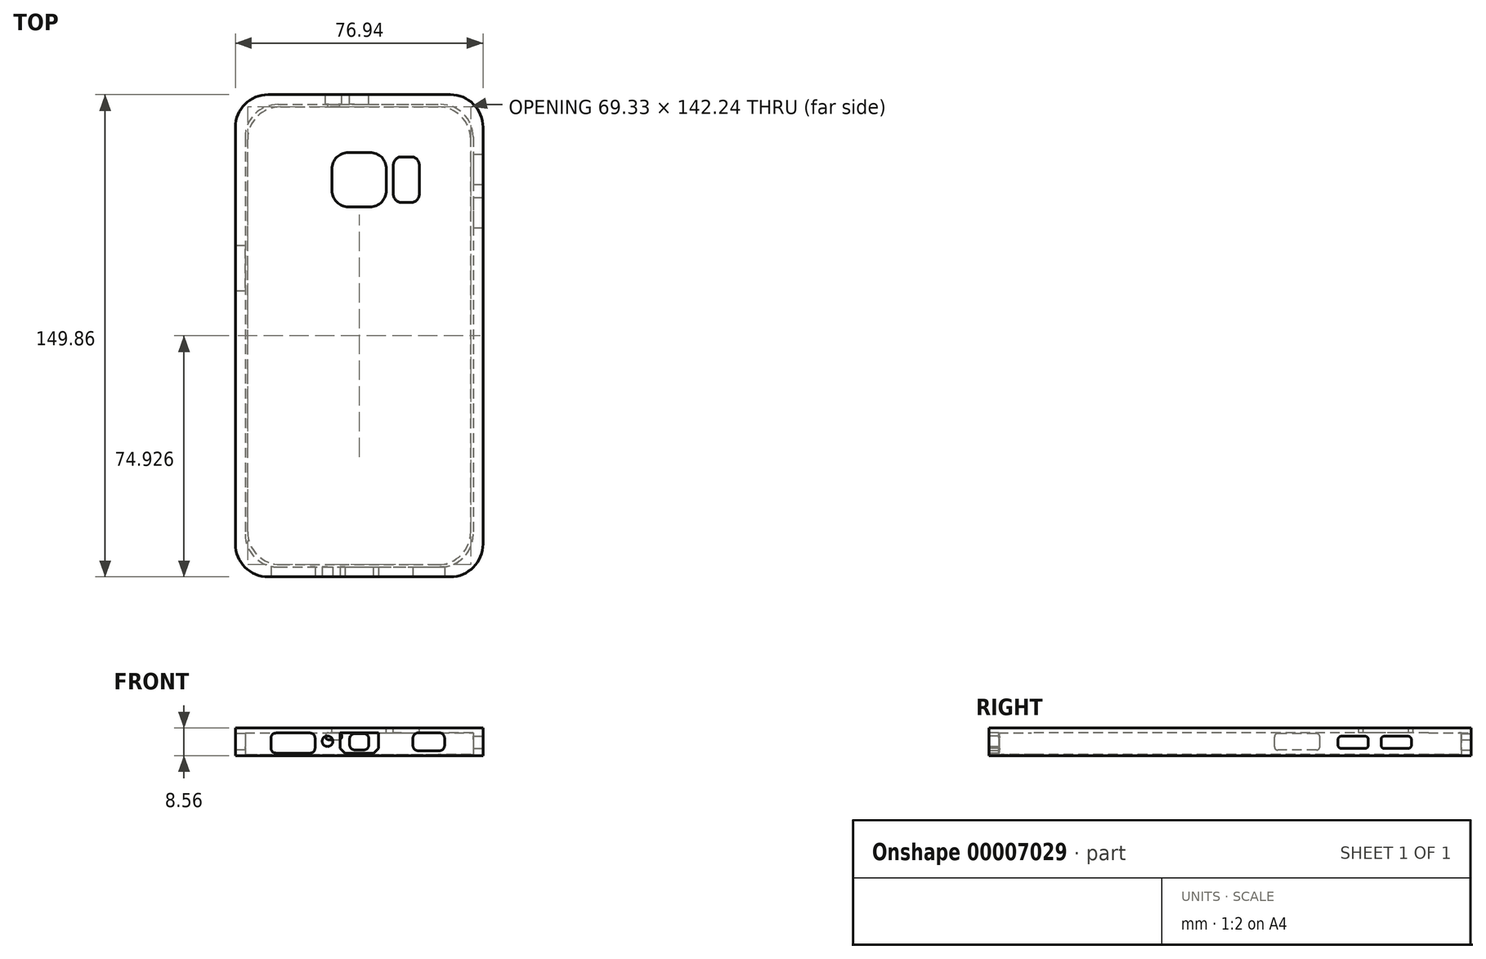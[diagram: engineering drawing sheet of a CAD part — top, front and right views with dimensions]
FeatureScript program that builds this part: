
annotation { "Feature Type Name" : "Feature", "Feature Type Description" : "" }
export const myFeature = defineFeature(function(context is Context, id is Id, definition is map)
    precondition{}
    {
        {
            var Q0;
            Q0=qCreatedBy(makeId("Top.planeOp"),FACE);
            var sketch = newSketch(context, id + "F0", { "sketchPlane" : qUnion([Q0])});
            skLineSegment(sketch, "E0.bottom", {"start": v(-42.48, 64.65) * mm, "end": v(28.37, 64.65) * mm});
            skLineSegment(sketch, "E0.top", {"start": v(-42.48, -79.12) * mm, "end": v(28.37, -79.12) * mm});
            skLineSegment(sketch, "E0.left", {"start": v(-42.48, 64.65) * mm, "end": v(-42.48, -79.12) * mm});
            skLineSegment(sketch, "E0.right", {"start": v(28.37, 64.65) * mm, "end": v(28.37, -79.12) * mm});
            skLineSegment(sketch, "E1.bottom", {"start": v(-45.53, 67.7) * mm, "end": v(31.41, 67.7) * mm});
            skLineSegment(sketch, "E1.top", {"start": v(-45.53, -82.16) * mm, "end": v(31.41, -82.16) * mm});
            skLineSegment(sketch, "E1.left", {"start": v(-45.53, 67.7) * mm, "end": v(-45.53, -82.16) * mm});
            skLineSegment(sketch, "E1.right", {"start": v(31.41, 67.7) * mm, "end": v(31.41, -82.16) * mm});
            skPoint(sketch, "E2", {"position": v(-7.06, 67.7) * mm});
            skPoint(sketch, "E3", {"position": v(-7.06, 64.65) * mm});
            skLineSegment(sketch, "E4", {"start": v(-7.06, 67.7) * mm, "end": v(-7.06, 64.65) * mm, "construction": true});
            skLineSegment(sketch, "E5", {"start": v(-7.06, -79.12) * mm, "end": v(-7.06, -82.16) * mm, "construction": true});
            skLineSegment(sketch, "E6", {"start": v(28.37, -7.23) * mm, "end": v(31.41, -7.23) * mm, "construction": true});
            skLineSegment(sketch, "E7", {"start": v(-42.48, -7.23) * mm, "end": v(-45.53, -7.23) * mm, "construction": true});
            skLineSegment(sketch, "E8.bottom", {"start": v(-31.56, -78.35) * mm, "end": v(17.44, -78.35) * mm});
            skLineSegment(sketch, "E8.top", {"start": v(-31.56, 63.89) * mm, "end": v(17.44, 63.89) * mm});
            skLineSegment(sketch, "E8.left", {"start": v(-41.72, -68.2) * mm, "end": v(-41.72, 53.73) * mm});
            skLineSegment(sketch, "E8.right", {"start": v(27.6, -68.2) * mm, "end": v(27.6, 53.73) * mm});
            skLineSegment(sketch, "E9", {"start": v(-7.06, -79.12) * mm, "end": v(-7.06, -78.35) * mm, "construction": true});
            skLineSegment(sketch, "E10", {"start": v(28.37, -7.23) * mm, "end": v(27.6, -7.23) * mm, "construction": true});
            skPoint(sketch, "E11.visualSharp", {"position": v(27.6, -78.35) * mm});
            skArc(sketch, "E11.filletArc", {"start": v(17.44, -78.35) * mm, "mid": v(24.63, -75.38) * mm, "end": v(27.6, -68.2) * mm});
            skPoint(sketch, "E12.visualSharp", {"position": v(-41.72, -78.35) * mm});
            skArc(sketch, "E12.filletArc", {"start": v(-41.72, -68.2) * mm, "mid": v(-38.75, -75.38) * mm, "end": v(-31.56, -78.35) * mm});
            skPoint(sketch, "E13.visualSharp", {"position": v(-41.72, 63.89) * mm});
            skArc(sketch, "E13.filletArc", {"start": v(-31.56, 63.89) * mm, "mid": v(-38.75, 60.91) * mm, "end": v(-41.72, 53.73) * mm});
            skPoint(sketch, "E14.visualSharp", {"position": v(27.6, 63.89) * mm});
            skArc(sketch, "E14.filletArc", {"start": v(27.6, 53.73) * mm, "mid": v(24.63, 60.91) * mm, "end": v(17.44, 63.89) * mm});
            skSolve(sketch);
        }
        {
            var Q0;
            Q0 = qSketchRegion(id + "F0", true);
            var Q1;
            Q1=makeQuery(id+"F0.imprint","IMPRINT",FACE,{"disambiguationData":[TD([[makeQuery(id+"F0.imprint","IMPRINT",EDGE,{"derivedFrom":sQuery(id+"F0.wireOp",EDGE,"E8.bottom")}),1.0]])]});
            var Q2;
            Q2=makeQuery(id+"F0.imprint","IMPRINT",FACE,{"disambiguationData":[TD([[makeQuery(id+"F0.imprint","IMPRINT",EDGE,{"derivedFrom":sQuery(id+"F0.wireOp",EDGE,"E0.bottom")}),-1.0]])]});
            extrude(context, id + "F1", {"entities" : qUnion([Q0, Q1, Q2]), "depth" : 8.56 * mm});
        }
        {
            var Q0;
            Q0=makeQuery(id+"F0.imprint","IMPRINT",FACE,{"disambiguationData":[TD([[makeQuery(id+"F0.imprint","IMPRINT",EDGE,{"derivedFrom":sQuery(id+"F0.wireOp",EDGE,"E8.bottom")}),1.0]])]});
            var Q1;
            Q1=makeQuery(id+"F0.imprint","IMPRINT",FACE,{"disambiguationData":[TD([[makeQuery(id+"F0.imprint","IMPRINT",EDGE,{"derivedFrom":sQuery(id+"F0.wireOp",EDGE,"E0.bottom")}),-1.0]])]});
            extrude(context, id + "F2", {"entities" : qUnion([Q0, Q1]), "operationType" : NewBodyOperationType.REMOVE, "depth" : 7.04 * mm});
        }
        {
            var Q0;
            Q0=makeQuery(id+"F2.boolean.opBoolean","COPY",EDGE,{"derivedFrom":makeQuery(id+"F2.opExtrude","SWEPT_EDGE",EDGE,{"disambiguationData":[OSD([sQuery(id+"F0.wireOp",EDGE,"E8.bottom"),sQuery(id+"F0.wireOp",EDGE,"E8.left")])]})});
            var Q1;
            Q1=makeQuery(id+"F2.boolean.opBoolean","COPY",EDGE,{"derivedFrom":makeQuery(id+"F2.opExtrude","SWEPT_EDGE",EDGE,{"disambiguationData":[OSD([sQuery(id+"F0.wireOp",EDGE,"E8.bottom"),sQuery(id+"F0.wireOp",EDGE,"E8.right")])]})});
            var Q2;
            Q2=makeQuery(id+"F2.boolean.opBoolean","COPY",EDGE,{"derivedFrom":makeQuery(id+"F2.opExtrude","SWEPT_EDGE",EDGE,{"disambiguationData":[OSD([sQuery(id+"F0.wireOp",EDGE,"E8.top"),sQuery(id+"F0.wireOp",EDGE,"E8.left")])]})});
            var Q3;
            Q3=makeQuery(id+"F2.boolean.opBoolean","COPY",EDGE,{"derivedFrom":makeQuery(id+"F2.opExtrude","SWEPT_EDGE",EDGE,{"disambiguationData":[OSD([sQuery(id+"F0.wireOp",EDGE,"E8.top"),sQuery(id+"F0.wireOp",EDGE,"E8.right")])]})});
            var Q4;
            Q4=makeQuery(id+"F1.opExtrude","SWEPT_EDGE",EDGE,{"disambiguationData":[OSD([sQuery(id+"F0.wireOp",EDGE,"E1.bottom"),sQuery(id+"F0.wireOp",EDGE,"E1.right")])]});
            var Q5;
            Q5=makeQuery(id+"F1.opExtrude","SWEPT_EDGE",EDGE,{"disambiguationData":[OSD([sQuery(id+"F0.wireOp",EDGE,"E1.top"),sQuery(id+"F0.wireOp",EDGE,"E1.right")])]});
            var Q6;
            Q6=makeQuery(id+"F1.opExtrude","SWEPT_EDGE",EDGE,{"disambiguationData":[OSD([sQuery(id+"F0.wireOp",EDGE,"E1.top"),sQuery(id+"F0.wireOp",EDGE,"E1.left")])]});
            var Q7;
            Q7=makeQuery(id+"F1.opExtrude","SWEPT_EDGE",EDGE,{"disambiguationData":[OSD([sQuery(id+"F0.wireOp",EDGE,"E1.bottom"),sQuery(id+"F0.wireOp",EDGE,"E1.left")])]});
            var Q8;
            Q8=makeQuery(id+"F2.boolean.opBoolean","COPY",EDGE,{"derivedFrom":makeQuery(id+"F2.opExtrude","SWEPT_EDGE",EDGE,{"disambiguationData":[OSD([sQuery(id+"F0.wireOp",EDGE,"E0.bottom"),sQuery(id+"F0.wireOp",EDGE,"E0.right")])]})});
            var Q9;
            Q9=makeQuery(id+"F2.boolean.opBoolean","COPY",EDGE,{"derivedFrom":makeQuery(id+"F2.opExtrude","SWEPT_EDGE",EDGE,{"disambiguationData":[OSD([sQuery(id+"F0.wireOp",EDGE,"E0.bottom"),sQuery(id+"F0.wireOp",EDGE,"E0.left")])]})});
            var Q10;
            Q10=makeQuery(id+"F2.boolean.opBoolean","COPY",EDGE,{"derivedFrom":makeQuery(id+"F2.opExtrude","SWEPT_EDGE",EDGE,{"disambiguationData":[OSD([sQuery(id+"F0.wireOp",EDGE,"E0.top"),sQuery(id+"F0.wireOp",EDGE,"E0.left")])]})});
            var Q11;
            Q11=makeQuery(id+"F2.boolean.opBoolean","COPY",EDGE,{"derivedFrom":makeQuery(id+"F2.opExtrude","SWEPT_EDGE",EDGE,{"disambiguationData":[OSD([sQuery(id+"F0.wireOp",EDGE,"E0.top"),sQuery(id+"F0.wireOp",EDGE,"E0.right")])]})});
            fillet(context, id + "F3", {"entities" : qUnion([Q0, Q1, Q2, Q3, Q4, Q5, Q6, Q7, Q8, Q9, Q10, Q11]), "radius" : 10.16 * mm, "tangentPropagation" : true, "allowEdgeOverflow" : false});
        }
        {
            var Q0;
            Q0=makeQuery(id+"F0.imprint","IMPRINT",FACE,{"disambiguationData":[TD([[makeQuery(id+"F0.imprint","IMPRINT",EDGE,{"derivedFrom":sQuery(id+"F0.wireOp",EDGE,"E0.bottom")}),-1.0]])]});
            extrude(context, id + "F4", {"entities" : qUnion([Q0]), "operationType" : NewBodyOperationType.ADD, "depth" : 0.38 * mm});
        }
        {
            var Q0;
            Q0=makeQuery(id+"F1.opExtrude","CAP_FACE",FACE,{"disambiguationData":[OSD([sQuery(id+"F0.wireOp",EDGE,"E1.bottom"),sQuery(id+"F0.wireOp",EDGE,"E1.top"),sQuery(id+"F0.wireOp",EDGE,"E1.left"),sQuery(id+"F0.wireOp",EDGE,"E1.right")])],"isStart":false});
            var sketch = newSketch(context, id + "F5", { "sketchPlane" : qUnion([Q0])});
            skLineSegment(sketch, "E15.bottom", {"start": v(-15.5, 49.71) * mm, "end": v(1.39, 49.71) * mm});
            skLineSegment(sketch, "E15.top", {"start": v(-15.5, 32.82) * mm, "end": v(1.39, 32.82) * mm});
            skLineSegment(sketch, "E15.left", {"start": v(-15.5, 49.71) * mm, "end": v(-15.5, 32.82) * mm});
            skLineSegment(sketch, "E15.right", {"start": v(1.39, 49.71) * mm, "end": v(1.39, 32.82) * mm});
            skLineSegment(sketch, "E16", {"start": v(-15.5, 41.27) * mm, "end": v(-45.53, 41.27) * mm, "construction": true});
            skLineSegment(sketch, "E17", {"start": v(1.39, 41.27) * mm, "end": v(31.41, 41.27) * mm, "construction": true});
            skLineSegment(sketch, "E18.bottom", {"start": v(3.55, 48.34) * mm, "end": v(11.62, 48.34) * mm});
            skLineSegment(sketch, "E18.top", {"start": v(3.55, 34.2) * mm, "end": v(11.62, 34.2) * mm});
            skLineSegment(sketch, "E18.left", {"start": v(3.55, 48.34) * mm, "end": v(3.55, 34.2) * mm});
            skLineSegment(sketch, "E18.right", {"start": v(11.62, 48.34) * mm, "end": v(11.62, 34.2) * mm});
            skLineSegment(sketch, "E19", {"start": v(8.73, 48.34) * mm, "end": v(8.73, 41.27) * mm, "construction": true});
            skLineSegment(sketch, "E20", {"start": v(4.69, 41.27) * mm, "end": v(4.69, 34.2) * mm, "construction": true});
            skSolve(sketch);
        }
        {
            var Q0;
            Q0 = qSketchRegion(id + "F5", true);
            extrude(context, id + "F6", {"entities" : qUnion([Q0]), "operationType" : NewBodyOperationType.REMOVE, "oppositeDirection" : true, "depth" : 25.4 * mm});
        }
        {
            var Q0;
            Q0=makeQuery(id+"F6.boolean.opBoolean","COPY",EDGE,{"derivedFrom":makeQuery(id+"F6.opExtrude","SWEPT_EDGE",EDGE,{"disambiguationData":[OSD([sQuery(id+"F5.wireOp",EDGE,"E15.bottom"),sQuery(id+"F5.wireOp",EDGE,"E15.left")])]})});
            var Q1;
            Q1=makeQuery(id+"F6.boolean.opBoolean","COPY",EDGE,{"derivedFrom":makeQuery(id+"F6.opExtrude","SWEPT_EDGE",EDGE,{"disambiguationData":[OSD([sQuery(id+"F5.wireOp",EDGE,"E15.bottom"),sQuery(id+"F5.wireOp",EDGE,"E15.right")])]})});
            var Q2;
            Q2=makeQuery(id+"F6.boolean.opBoolean","COPY",EDGE,{"derivedFrom":makeQuery(id+"F6.opExtrude","SWEPT_EDGE",EDGE,{"disambiguationData":[OSD([sQuery(id+"F5.wireOp",EDGE,"E15.top"),sQuery(id+"F5.wireOp",EDGE,"E15.right")])]})});
            var Q3;
            Q3=makeQuery(id+"F6.boolean.opBoolean","COPY",EDGE,{"derivedFrom":makeQuery(id+"F6.opExtrude","SWEPT_EDGE",EDGE,{"disambiguationData":[OSD([sQuery(id+"F5.wireOp",EDGE,"E15.top"),sQuery(id+"F5.wireOp",EDGE,"E15.left")])]})});
            fillet(context, id + "F7", {"entities" : qUnion([Q0, Q1, Q2, Q3]), "radius" : 5.08 * mm, "tangentPropagation" : true, "allowEdgeOverflow" : false});
        }
        {
            var Q0;
            Q0=makeQuery(id+"F6.boolean.opBoolean","COPY",EDGE,{"derivedFrom":makeQuery(id+"F6.opExtrude","SWEPT_EDGE",EDGE,{"disambiguationData":[OSD([sQuery(id+"F5.wireOp",EDGE,"E18.bottom"),sQuery(id+"F5.wireOp",EDGE,"E18.right")])]})});
            var Q1;
            Q1=makeQuery(id+"F6.boolean.opBoolean","COPY",EDGE,{"derivedFrom":makeQuery(id+"F6.opExtrude","SWEPT_EDGE",EDGE,{"disambiguationData":[OSD([sQuery(id+"F5.wireOp",EDGE,"E18.bottom"),sQuery(id+"F5.wireOp",EDGE,"E18.left")])]})});
            var Q2;
            Q2=makeQuery(id+"F6.boolean.opBoolean","COPY",EDGE,{"derivedFrom":makeQuery(id+"F6.opExtrude","SWEPT_EDGE",EDGE,{"disambiguationData":[OSD([sQuery(id+"F5.wireOp",EDGE,"E18.top"),sQuery(id+"F5.wireOp",EDGE,"E18.right")])]})});
            var Q3;
            Q3=makeQuery(id+"F6.boolean.opBoolean","COPY",EDGE,{"derivedFrom":makeQuery(id+"F6.opExtrude","SWEPT_EDGE",EDGE,{"disambiguationData":[OSD([sQuery(id+"F5.wireOp",EDGE,"E18.top"),sQuery(id+"F5.wireOp",EDGE,"E18.left")])]})});
            fillet(context, id + "F8", {"entities" : qUnion([Q0, Q1, Q2, Q3]), "radius" : 2.54 * mm, "tangentPropagation" : true, "allowEdgeOverflow" : false});
        }
        {
            var Q0;
            Q0=makeQuery(id+"F1.opExtrude","SWEPT_FACE",FACE,{"disambiguationData":[OSD([sQuery(id+"F0.wireOp",EDGE,"E1.left")])]});
            var sketch = newSketch(context, id + "F9", { "sketchPlane" : qUnion([Q0])});
            skLineSegment(sketch, "E21.bottom", {"start": v(-20.68, 1.74) * mm, "end": v(-6.58, 1.74) * mm});
            skLineSegment(sketch, "E21.top", {"start": v(-20.68, 6.82) * mm, "end": v(-6.58, 6.82) * mm});
            skLineSegment(sketch, "E21.left", {"start": v(-20.68, 1.74) * mm, "end": v(-20.68, 6.82) * mm});
            skLineSegment(sketch, "E21.right", {"start": v(-6.58, 1.74) * mm, "end": v(-6.58, 6.82) * mm});
            skLineSegment(sketch, "E22", {"start": v(-13.63, 6.82) * mm, "end": v(-13.63, 8.56) * mm, "construction": true});
            skLineSegment(sketch, "E23", {"start": v(-13.63, 1.74) * mm, "end": v(-13.63, 0) * mm, "construction": true});
            skSolve(sketch);
        }
        {
            var Q0;
            Q0 = qSketchRegion(id + "F9", true);
            extrude(context, id + "F10", {"entities" : qUnion([Q0]), "operationType" : NewBodyOperationType.REMOVE, "oppositeDirection" : true, "depth" : 25.4 * mm});
        }
        {
            var Q0;
            Q0=makeQuery(id+"F10.boolean.opBoolean","COPY",EDGE,{"derivedFrom":makeQuery(id+"F10.opExtrude","SWEPT_EDGE",EDGE,{"disambiguationData":[OSD([sQuery(id+"F9.wireOp",EDGE,"E21.bottom"),sQuery(id+"F9.wireOp",EDGE,"E21.left")])]})});
            var Q1;
            Q1=makeQuery(id+"F10.boolean.opBoolean","COPY",EDGE,{"derivedFrom":makeQuery(id+"F10.opExtrude","SWEPT_EDGE",EDGE,{"disambiguationData":[OSD([sQuery(id+"F9.wireOp",EDGE,"E21.top"),sQuery(id+"F9.wireOp",EDGE,"E21.left")])]})});
            var Q2;
            Q2=makeQuery(id+"F10.boolean.opBoolean","COPY",EDGE,{"derivedFrom":makeQuery(id+"F10.opExtrude","SWEPT_EDGE",EDGE,{"disambiguationData":[OSD([sQuery(id+"F9.wireOp",EDGE,"E21.bottom"),sQuery(id+"F9.wireOp",EDGE,"E21.right")])]})});
            var Q3;
            Q3=makeQuery(id+"F10.boolean.opBoolean","COPY",EDGE,{"derivedFrom":makeQuery(id+"F10.opExtrude","SWEPT_EDGE",EDGE,{"disambiguationData":[OSD([sQuery(id+"F9.wireOp",EDGE,"E21.top"),sQuery(id+"F9.wireOp",EDGE,"E21.right")])]})});
            fillet(context, id + "F11", {"entities" : qUnion([Q0, Q1, Q2, Q3]), "radius" : 1.02 * mm, "tangentPropagation" : true, "allowEdgeOverflow" : false});
        }
        {
            var Q0;
            Q0=makeQuery(id+"F1.opExtrude","SWEPT_FACE",FACE,{"disambiguationData":[OSD([sQuery(id+"F0.wireOp",EDGE,"E1.top")])]});
            var sketch = newSketch(context, id + "F12", { "sketchPlane" : qUnion([Q0])});
            skLineSegment(sketch, "E24.bottom", {"start": v(-1.09, 0.76) * mm, "end": v(-13.03, 0.76) * mm});
            skLineSegment(sketch, "E24.top", {"start": v(-1.09, 7.04) * mm, "end": v(-13.03, 7.04) * mm});
            skLineSegment(sketch, "E24.left", {"start": v(-1.09, 0.76) * mm, "end": v(-1.09, 7.04) * mm});
            skLineSegment(sketch, "E24.right", {"start": v(-13.03, 0.76) * mm, "end": v(-13.03, 7.04) * mm});
            skLineSegment(sketch, "E25", {"start": v(-45.53, 0) * mm, "end": v(-45.53, 7.04) * mm, "construction": true});
            skLineSegment(sketch, "E26", {"start": v(31.41, 7.04) * mm, "end": v(31.41, 0) * mm, "construction": true});
            skLineSegment(sketch, "E27", {"start": v(-45.53, 7.04) * mm, "end": v(31.41, 7.04) * mm, "construction": true});
            skPoint(sketch, "E28", {"position": v(-7.06, 7.04) * mm});
            skCircle(sketch, "E29", {"center": v(-16.9, 4.46) * mm, "radius": 1.65 * mm});
            skLineSegment(sketch, "E30", {"start": v(-45.53, 3.52) * mm, "end": v(31.41, 3.52) * mm, "construction": true});
            skLineSegment(sketch, "E31.bottom", {"start": v(-20.8, 0.77) * mm, "end": v(-34.48, 0.77) * mm});
            skLineSegment(sketch, "E31.top", {"start": v(-20.8, 7) * mm, "end": v(-34.48, 7) * mm});
            skLineSegment(sketch, "E31.left", {"start": v(-20.8, 0.77) * mm, "end": v(-20.8, 7) * mm});
            skLineSegment(sketch, "E31.right", {"start": v(-34.48, 0.77) * mm, "end": v(-34.48, 7) * mm});
            skLineSegment(sketch, "E32.bottom", {"start": v(19.45, 1.52) * mm, "end": v(9.65, 1.52) * mm});
            skLineSegment(sketch, "E32.top", {"start": v(19.45, 7.04) * mm, "end": v(9.65, 7.04) * mm});
            skLineSegment(sketch, "E32.left", {"start": v(19.45, 1.52) * mm, "end": v(19.45, 7.04) * mm});
            skLineSegment(sketch, "E32.right", {"start": v(9.65, 1.52) * mm, "end": v(9.65, 7.04) * mm});
            skSolve(sketch);
        }
        {
            var Q0;
            Q0=makeQuery(id+"F12.imprint","IMPRINT",FACE,{"disambiguationData":[TD([[makeQuery(id+"F12.imprint","IMPRINT",EDGE,{"derivedFrom":sQuery(id+"F12.wireOp",EDGE,"E31.bottom")}),-1.0]])]});
            var Q1;
            Q1=makeQuery(id+"F12.imprint","IMPRINT",FACE,{"disambiguationData":[TD([[makeQuery(id+"F12.imprint","IMPRINT",EDGE,{"derivedFrom":sQuery(id+"F12.wireOp",EDGE,"E24.bottom")}),-1.0]])]});
            var Q2;
            Q2=makeQuery(id+"F12.imprint","IMPRINT",FACE,{"disambiguationData":[TD([[makeQuery(id+"F12.imprint","IMPRINT",EDGE,{"derivedFrom":sQuery(id+"F12.wireOp",EDGE,"E29")}),1.0]])]});
            var Q3;
            Q3=makeQuery(id+"F12.imprint","IMPRINT",FACE,{"disambiguationData":[TD([[makeQuery(id+"F12.imprint","IMPRINT",EDGE,{"derivedFrom":sQuery(id+"F12.wireOp",EDGE,"f402ad22-fe28-4430-b61b-633b21e1cf4e")}),1.0]])]});
            extrude(context, id + "F13", {"entities" : qUnion([Q0, Q1, Q2, Q3]), "operationType" : NewBodyOperationType.REMOVE, "oppositeDirection" : true, "depth" : 25.4 * mm});
        }
        {
            var Q0;
            Q0=makeQuery(id+"F1.opExtrude","SWEPT_FACE",FACE,{"disambiguationData":[OSD([sQuery(id+"F0.wireOp",EDGE,"E1.right")])]});
            var sketch = newSketch(context, id + "F14", { "sketchPlane" : qUnion([Q0])});
            skLineSegment(sketch, "E33.bottom", {"start": v(49.15, 6.02) * mm, "end": v(39.73, 6.02) * mm});
            skLineSegment(sketch, "E33.top", {"start": v(49.15, 2.2) * mm, "end": v(39.73, 2.2) * mm});
            skLineSegment(sketch, "E33.left", {"start": v(49.15, 6.02) * mm, "end": v(49.15, 2.2) * mm});
            skLineSegment(sketch, "E33.right", {"start": v(39.73, 6.02) * mm, "end": v(39.73, 2.2) * mm});
            skLineSegment(sketch, "E34.bottom", {"start": v(35.77, 6.02) * mm, "end": v(26.34, 6.02) * mm});
            skLineSegment(sketch, "E34.top", {"start": v(35.77, 2.2) * mm, "end": v(26.34, 2.2) * mm});
            skLineSegment(sketch, "E34.left", {"start": v(35.77, 6.02) * mm, "end": v(35.77, 2.2) * mm});
            skLineSegment(sketch, "E34.right", {"start": v(26.34, 6.02) * mm, "end": v(26.34, 2.2) * mm});
            skPoint(sketch, "E35.endSnap0", {"position": v(31.06, 6.02) * mm});
            skSolve(sketch);
        }
        {
            var Q0;
            Q0 = qSketchRegion(id + "F12", true);
            extrude(context, id + "F15", {"entities" : qUnion([Q0]), "operationType" : NewBodyOperationType.REMOVE, "oppositeDirection" : true, "depth" : 25.4 * mm});
        }
        {
            var Q0;
            Q0=makeQuery(id+"F15.boolean.opBoolean","COPY",EDGE,{"derivedFrom":makeQuery(id+"F15.opExtrude","SWEPT_EDGE",EDGE,{"disambiguationData":[OSD([sQuery(id+"F12.wireOp",EDGE,"E32.bottom"),sQuery(id+"F12.wireOp",EDGE,"E32.left")])]})});
            var Q1;
            Q1=makeQuery(id+"F15.boolean.opBoolean","COPY",EDGE,{"derivedFrom":makeQuery(id+"F15.opExtrude","SWEPT_EDGE",EDGE,{"disambiguationData":[OSD([sQuery(id+"F12.wireOp",EDGE,"E32.bottom"),sQuery(id+"F12.wireOp",EDGE,"E32.right")])]})});
            var Q2;
            Q2=makeQuery(id+"F15.boolean.opBoolean","COPY",EDGE,{"derivedFrom":makeQuery(id+"F15.opExtrude","SWEPT_EDGE",EDGE,{"disambiguationData":[OSD([sQuery(id+"F12.wireOp",EDGE,"E32.top"),sQuery(id+"F12.wireOp",EDGE,"E32.left")])]})});
            var Q3;
            Q3=makeQuery(id+"F15.boolean.opBoolean","COPY",EDGE,{"derivedFrom":makeQuery(id+"F15.opExtrude","SWEPT_EDGE",EDGE,{"disambiguationData":[OSD([sQuery(id+"F12.wireOp",EDGE,"E32.top"),sQuery(id+"F12.wireOp",EDGE,"E32.right")])]})});
            fillet(context, id + "F16", {"entities" : qUnion([Q0, Q1, Q2, Q3]), "radius" : 1.52 * mm, "tangentPropagation" : true, "allowEdgeOverflow" : false});
        }
        {
            var Q0;
            Q0=makeQuery(id+"F13.boolean.opBoolean","COPY",EDGE,{"derivedFrom":makeQuery(id+"F13.opExtrude","SWEPT_EDGE",EDGE,{"disambiguationData":[OSD([sQuery(id+"F12.wireOp",EDGE,"E24.bottom"),sQuery(id+"F12.wireOp",EDGE,"E24.right")])]})});
            var Q1;
            Q1=makeQuery(id+"F13.boolean.opBoolean","COPY",EDGE,{"derivedFrom":makeQuery(id+"F13.opExtrude","SWEPT_EDGE",EDGE,{"disambiguationData":[OSD([sQuery(id+"F12.wireOp",EDGE,"E24.bottom"),sQuery(id+"F12.wireOp",EDGE,"E24.left")])]})});
            chamfer(context, id + "F17", {"entities" : qUnion([Q0, Q1]), "width" : 1.52 * mm, "tangentPropagation" : true});
        }
        {
            var Q0;
            Q0=makeQuery(id+"F13.boolean.opBoolean","COPY",EDGE,{"derivedFrom":makeQuery(id+"F13.opExtrude","SWEPT_EDGE",EDGE,{"disambiguationData":[OSD([sQuery(id+"F12.wireOp",EDGE,"E31.top"),sQuery(id+"F12.wireOp",EDGE,"E31.left")])]})});
            var Q1;
            Q1=makeQuery(id+"F13.boolean.opBoolean","COPY",EDGE,{"derivedFrom":makeQuery(id+"F13.opExtrude","SWEPT_EDGE",EDGE,{"disambiguationData":[OSD([sQuery(id+"F12.wireOp",EDGE,"E31.top"),sQuery(id+"F12.wireOp",EDGE,"E31.right")])]})});
            var Q2;
            Q2=makeQuery(id+"F13.boolean.opBoolean","COPY",EDGE,{"derivedFrom":makeQuery(id+"F13.opExtrude","SWEPT_EDGE",EDGE,{"disambiguationData":[OSD([sQuery(id+"F12.wireOp",EDGE,"E31.bottom"),sQuery(id+"F12.wireOp",EDGE,"E31.right")])]})});
            var Q3;
            Q3=makeQuery(id+"F13.boolean.opBoolean","COPY",EDGE,{"derivedFrom":makeQuery(id+"F13.opExtrude","SWEPT_EDGE",EDGE,{"disambiguationData":[OSD([sQuery(id+"F12.wireOp",EDGE,"E31.bottom"),sQuery(id+"F12.wireOp",EDGE,"E31.left")])]})});
            fillet(context, id + "F18", {"entities" : qUnion([Q0, Q1, Q2, Q3]), "radius" : 1.52 * mm, "tangentPropagation" : true, "allowEdgeOverflow" : false});
        }
        {
            var Q0;
            Q0=makeQuery(id+"F1.opExtrude","SWEPT_FACE",FACE,{"disambiguationData":[OSD([sQuery(id+"F0.wireOp",EDGE,"E1.bottom")])]});
            var sketch = newSketch(context, id + "F19", { "sketchPlane" : qUnion([Q0])});
            skLineSegment(sketch, "E36", {"start": v(35.37, 4.28) * mm, "end": v(-21.25, 4.28) * mm, "construction": true});
            skLineSegment(sketch, "E37.rect.bottom", {"start": v(10.05, 1.77) * mm, "end": v(4.07, 1.77) * mm});
            skLineSegment(sketch, "E37.rect.top", {"start": v(10.05, 6.79) * mm, "end": v(4.07, 6.79) * mm});
            skLineSegment(sketch, "E37.rect.left", {"start": v(10.05, 1.77) * mm, "end": v(10.05, 6.79) * mm});
            skLineSegment(sketch, "E37.rect.right", {"start": v(4.07, 1.77) * mm, "end": v(4.07, 6.79) * mm});
            skPoint(sketch, "E37.rect.middle", {"position": v(7.06, 4.28) * mm});
            skLineSegment(sketch, "E38.rect.bottom", {"start": v(17.57, 4.9) * mm, "end": v(12.49, 4.9) * mm});
            skLineSegment(sketch, "E38.rect.top", {"start": v(17.57, 7.12) * mm, "end": v(12.49, 7.12) * mm});
            skLineSegment(sketch, "E38.rect.left", {"start": v(17.57, 4.9) * mm, "end": v(17.57, 7.12) * mm});
            skLineSegment(sketch, "E38.rect.right", {"start": v(12.49, 4.9) * mm, "end": v(12.49, 7.12) * mm});
            skPoint(sketch, "E38.rect.middle", {"position": v(15.03, 6.01) * mm});
            skSolve(sketch);
        }
        {
            var Q0;
            Q0 = qSketchRegion(id + "F19", true);
            extrude(context, id + "F20", {"entities" : qUnion([Q0]), "operationType" : NewBodyOperationType.REMOVE, "oppositeDirection" : true, "depth" : 3.8 * mm});
        }
        {
            var Q0;
            Q0=makeQuery(id+"F20.boolean.opBoolean","COPY",EDGE,{"derivedFrom":makeQuery(id+"F20.opExtrude","SWEPT_EDGE",EDGE,{"disambiguationData":[OSD([sQuery(id+"F19.wireOp",EDGE,"E37.rect.bottom"),sQuery(id+"F19.wireOp",EDGE,"E37.rect.right")])]})});
            var Q1;
            Q1=makeQuery(id+"F20.boolean.opBoolean","COPY",EDGE,{"derivedFrom":makeQuery(id+"F20.opExtrude","SWEPT_EDGE",EDGE,{"disambiguationData":[OSD([sQuery(id+"F19.wireOp",EDGE,"E37.rect.bottom"),sQuery(id+"F19.wireOp",EDGE,"E37.rect.left")])]})});
            var Q2;
            Q2=makeQuery(id+"F20.boolean.opBoolean","COPY",EDGE,{"derivedFrom":makeQuery(id+"F20.opExtrude","SWEPT_EDGE",EDGE,{"disambiguationData":[OSD([sQuery(id+"F19.wireOp",EDGE,"E37.rect.top"),sQuery(id+"F19.wireOp",EDGE,"E37.rect.left")])]})});
            var Q3;
            Q3=makeQuery(id+"F20.boolean.opBoolean","COPY",EDGE,{"derivedFrom":makeQuery(id+"F20.opExtrude","SWEPT_EDGE",EDGE,{"disambiguationData":[OSD([sQuery(id+"F19.wireOp",EDGE,"E37.rect.top"),sQuery(id+"F19.wireOp",EDGE,"E37.rect.right")])]})});
            fillet(context, id + "F21", {"entities" : qUnion([Q0, Q1, Q2, Q3]), "radius" : 1.52 * mm, "tangentPropagation" : true, "allowEdgeOverflow" : false});
        }
        {
            var Q0;
            Q0=makeQuery(id+"F20.boolean.opBoolean","COPY",EDGE,{"derivedFrom":makeQuery(id+"F20.opExtrude","SWEPT_EDGE",EDGE,{"disambiguationData":[OSD([sQuery(id+"F19.wireOp",EDGE,"E38.rect.bottom"),sQuery(id+"F19.wireOp",EDGE,"E38.rect.left")])]})});
            var Q1;
            Q1=makeQuery(id+"F20.boolean.opBoolean","COPY",EDGE,{"derivedFrom":makeQuery(id+"F20.opExtrude","SWEPT_EDGE",EDGE,{"disambiguationData":[OSD([sQuery(id+"F19.wireOp",EDGE,"E38.rect.bottom"),sQuery(id+"F19.wireOp",EDGE,"E38.rect.right")])]})});
            var Q2;
            Q2=makeQuery(id+"F20.boolean.opBoolean","COPY",EDGE,{"derivedFrom":makeQuery(id+"F20.opExtrude","SWEPT_EDGE",EDGE,{"disambiguationData":[OSD([sQuery(id+"F19.wireOp",EDGE,"E38.rect.top"),sQuery(id+"F19.wireOp",EDGE,"E38.rect.left")])]})});
            var Q3;
            Q3=makeQuery(id+"F20.boolean.opBoolean","COPY",EDGE,{"derivedFrom":makeQuery(id+"F20.opExtrude","SWEPT_EDGE",EDGE,{"disambiguationData":[OSD([sQuery(id+"F19.wireOp",EDGE,"E38.rect.top"),sQuery(id+"F19.wireOp",EDGE,"E38.rect.right")])]})});
            fillet(context, id + "F22", {"entities" : qUnion([Q0, Q1, Q2, Q3]), "radius" : 1.02 * mm, "tangentPropagation" : true, "allowEdgeOverflow" : false});
        }
        {
            var Q0;
            Q0 = qSketchRegion(id + "F14", true);
            extrude(context, id + "F23", {"entities" : qUnion([Q0]), "operationType" : NewBodyOperationType.REMOVE, "oppositeDirection" : true, "depth" : 25.4 * mm});
        }
        {
            var Q0;
            Q0=makeQuery(id+"F23.boolean.opBoolean","COPY",EDGE,{"derivedFrom":makeQuery(id+"F23.opExtrude","SWEPT_EDGE",EDGE,{"disambiguationData":[OSD([sQuery(id+"F14.wireOp",EDGE,"E34.bottom"),sQuery(id+"F14.wireOp",EDGE,"E34.left")])]})});
            var Q1;
            Q1=makeQuery(id+"F23.boolean.opBoolean","COPY",EDGE,{"derivedFrom":makeQuery(id+"F23.opExtrude","SWEPT_EDGE",EDGE,{"disambiguationData":[OSD([sQuery(id+"F14.wireOp",EDGE,"E34.bottom"),sQuery(id+"F14.wireOp",EDGE,"E34.right")])]})});
            var Q2;
            Q2=makeQuery(id+"F23.boolean.opBoolean","COPY",EDGE,{"derivedFrom":makeQuery(id+"F23.opExtrude","SWEPT_EDGE",EDGE,{"disambiguationData":[OSD([sQuery(id+"F14.wireOp",EDGE,"E34.top"),sQuery(id+"F14.wireOp",EDGE,"E34.right")])]})});
            var Q3;
            Q3=makeQuery(id+"F23.boolean.opBoolean","COPY",EDGE,{"derivedFrom":makeQuery(id+"F23.opExtrude","SWEPT_EDGE",EDGE,{"disambiguationData":[OSD([sQuery(id+"F14.wireOp",EDGE,"E34.top"),sQuery(id+"F14.wireOp",EDGE,"E34.left")])]})});
            var Q4;
            Q4=makeQuery(id+"F23.boolean.opBoolean","COPY",EDGE,{"derivedFrom":makeQuery(id+"F23.opExtrude","SWEPT_EDGE",EDGE,{"disambiguationData":[OSD([sQuery(id+"F14.wireOp",EDGE,"E33.top"),sQuery(id+"F14.wireOp",EDGE,"E33.right")])]})});
            var Q5;
            Q5=makeQuery(id+"F23.boolean.opBoolean","COPY",EDGE,{"derivedFrom":makeQuery(id+"F23.opExtrude","SWEPT_EDGE",EDGE,{"disambiguationData":[OSD([sQuery(id+"F14.wireOp",EDGE,"E33.bottom"),sQuery(id+"F14.wireOp",EDGE,"E33.right")])]})});
            var Q6;
            Q6=makeQuery(id+"F23.boolean.opBoolean","COPY",EDGE,{"derivedFrom":makeQuery(id+"F23.opExtrude","SWEPT_EDGE",EDGE,{"disambiguationData":[OSD([sQuery(id+"F14.wireOp",EDGE,"E33.top"),sQuery(id+"F14.wireOp",EDGE,"E33.left")])]})});
            var Q7;
            Q7=makeQuery(id+"F23.boolean.opBoolean","COPY",EDGE,{"derivedFrom":makeQuery(id+"F23.opExtrude","SWEPT_EDGE",EDGE,{"disambiguationData":[OSD([sQuery(id+"F14.wireOp",EDGE,"E33.bottom"),sQuery(id+"F14.wireOp",EDGE,"E33.left")])]})});
            fillet(context, id + "F24", {"entities" : qUnion([Q0, Q1, Q2, Q3, Q4, Q5, Q6, Q7]), "radius" : 1.02 * mm, "tangentPropagation" : true, "allowEdgeOverflow" : false});
        }
    });
